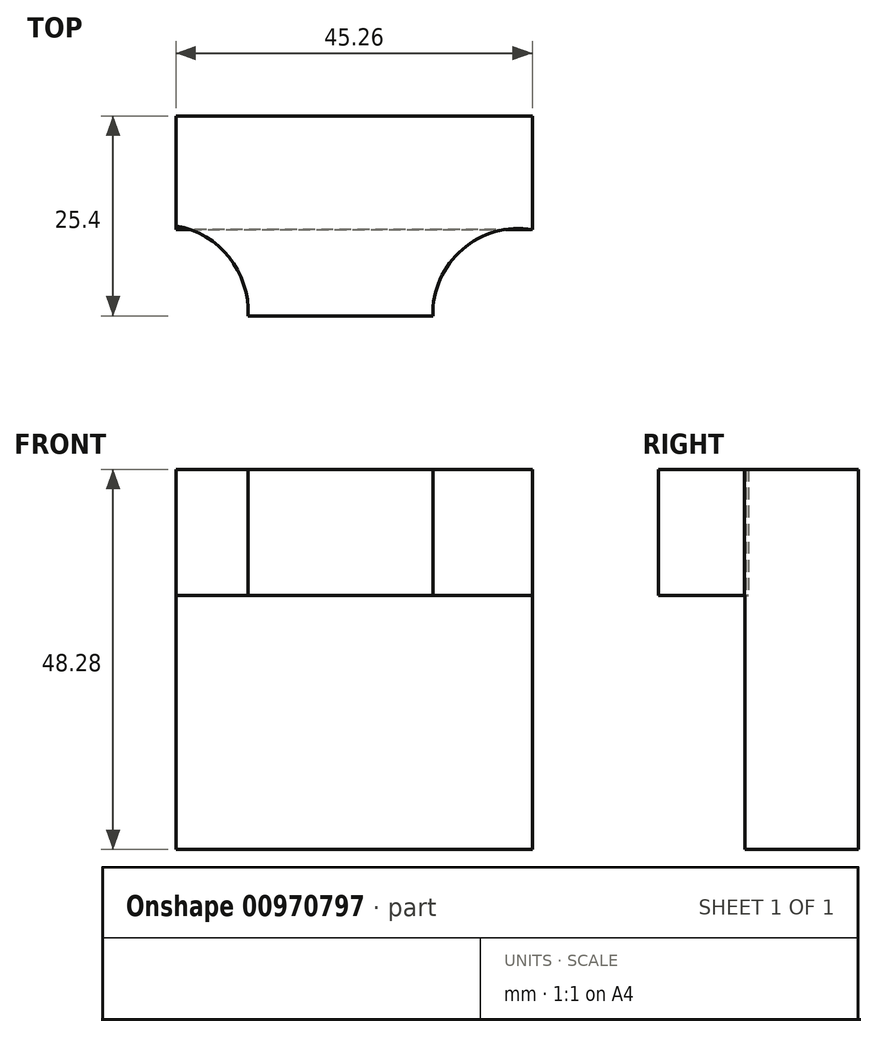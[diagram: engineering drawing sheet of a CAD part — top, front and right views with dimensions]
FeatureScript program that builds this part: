
annotation { "Feature Type Name" : "Feature", "Feature Type Description" : "" }
export const myFeature = defineFeature(function(context is Context, id is Id, definition is map)
    precondition{}
    {
        {
            var Q0;
            Q0=qCreatedBy(makeId("Front.planeOp"),FACE);
            var sketch = newSketch(context, id + "F0", { "sketchPlane" : qUnion([Q0])});
            skLineSegment(sketch, "E0.bottom", {"start": v(22.63, 16) * mm, "end": v(-22.63, 16) * mm});
            skLineSegment(sketch, "E0.top", {"start": v(22.63, -32.29) * mm, "end": v(-22.63, -32.29) * mm});
            skLineSegment(sketch, "E0.left", {"start": v(22.63, 16) * mm, "end": v(22.63, -32.29) * mm});
            skLineSegment(sketch, "E0.right", {"start": v(-22.63, 16) * mm, "end": v(-22.63, -32.29) * mm});
            skSolve(sketch);
        }
        {
            var Q0;
            Q0=makeQuery(id+"F0.imprint","IMPRINT",FACE,{"disambiguationData":[TD([[makeQuery(id+"F0.imprint","IMPRINT",EDGE,{"derivedFrom":sQuery(id+"F0.wireOp",EDGE,"E0.bottom")}),1.0]])]});
            extrude(context, id + "F1", {"entities" : qUnion([Q0]), "depth" : 25.4 * mm, "offsetDistance" : 25.4 * mm});
        }
        {
            var Q0;
            Q0=qCreatedBy(makeId("Top.planeOp"),FACE);
            var sketch = newSketch(context, id + "F2", { "sketchPlane" : qUnion([Q0])});
            skLineSegment(sketch, "E1.bottom", {"start": v(-27.35, -29.93) * mm, "end": v(25.87, -29.93) * mm});
            skLineSegment(sketch, "E1.top", {"start": v(-27.35, -14.41) * mm, "end": v(25.87, -14.41) * mm});
            skLineSegment(sketch, "E1.left", {"start": v(-27.35, -29.93) * mm, "end": v(-27.35, -14.41) * mm});
            skLineSegment(sketch, "E1.right", {"start": v(25.87, -29.93) * mm, "end": v(25.87, -14.41) * mm});
            skLineSegment(sketch, "E2.bottom", {"start": v(25.87, -14.41) * mm, "end": v(-27.35, -14.41) * mm});
            skLineSegment(sketch, "E2.top", {"start": v(25.87, -14.41) * mm, "end": v(-27.35, -14.41) * mm});
            skLineSegment(sketch, "E2.left", {"start": v(25.87, -14.41) * mm, "end": v(25.87, -14.41) * mm});
            skLineSegment(sketch, "E2.right", {"start": v(-27.35, -14.41) * mm, "end": v(-27.35, -14.41) * mm});
            skSolve(sketch);
        }
        {
            var Q0;
            Q0 = qSketchRegion(id + "F2", true);
            extrude(context, id + "F3", {"entities" : qUnion([Q0]), "operationType" : NewBodyOperationType.REMOVE, "oppositeDirection" : true, "depth" : 39.38 * mm, "offsetDistance" : 25.4 * mm});
        }
        {
            var Q0;
            Q0=qCreatedBy(makeId("Top.planeOp"),FACE);
            var sketch = newSketch(context, id + "F4", { "sketchPlane" : qUnion([Q0])});
            skCircle(sketch, "E3", {"center": v(20.87, -25.17) * mm, "radius": 10.89 * mm});
            skPoint(sketch, "E3.first.point", {"position": v(19.22, -14.41) * mm});
            skPoint(sketch, "E3.second.point", {"position": v(24.4, -35.48) * mm});
            skPoint(sketch, "E3.third.point", {"position": v(28.82, -17.74) * mm});
            skCircle(sketch, "E4", {"center": v(-24.5, -24.84) * mm, "radius": 11.04 * mm});
            skPoint(sketch, "E4.first.point", {"position": v(-19.96, -14.78) * mm});
            skPoint(sketch, "E4.second.point", {"position": v(-23.65, -35.85) * mm});
            skPoint(sketch, "E4.third.point", {"position": v(-34.74, -20.7) * mm});
            skSolve(sketch);
        }
        {
            var Q0;
            Q0 = qSketchRegion(id + "F4", true);
            var Q1;
            Q1=makeQuery(id+"F4.imprint","IMPRINT",FACE,{"disambiguationData":[TD([[makeQuery(id+"F4.imprint","IMPRINT",EDGE,{"derivedFrom":sQuery(id+"F4.wireOp",EDGE,"E4")}),1.0]])]});
            extrude(context, id + "F5", {"entities" : qUnion([Q0, Q1]), "operationType" : NewBodyOperationType.REMOVE, "depth" : 23.32 * mm, "offsetDistance" : 25.4 * mm});
        }
    });
